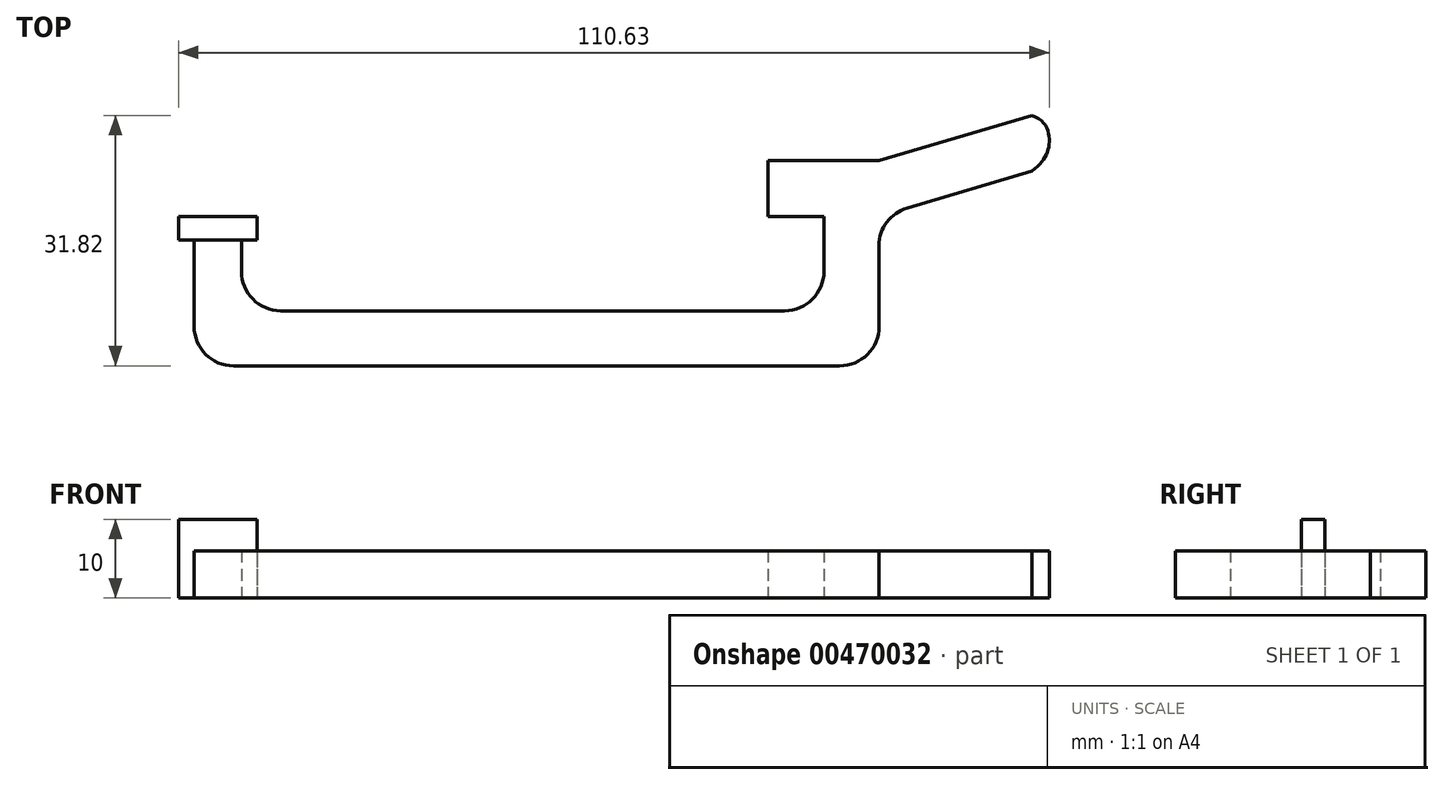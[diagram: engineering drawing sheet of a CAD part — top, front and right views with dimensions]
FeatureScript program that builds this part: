
annotation { "Feature Type Name" : "Feature", "Feature Type Description" : "" }
export const myFeature = defineFeature(function(context is Context, id is Id, definition is map)
    precondition{}
    {
        {
            var Q0;
            Q0=qCreatedBy(makeId("Top.planeOp"),FACE);
            var sketch = newSketch(context, id + "F0", { "sketchPlane" : qUnion([Q0])});
            skLineSegment(sketch, "E0.bottom", {"start": v(38.5, -3.5) * mm, "end": v(-38.5, -3.5) * mm});
            skLineSegment(sketch, "E0.top", {"start": v(38.5, 3.5) * mm, "end": v(-35.5, 3.5) * mm});
            skPoint(sketch, "E0.middle", {"position": v(0, 0) * mm});
            skLineSegment(sketch, "E1.top", {"start": v(-38.5, -3.5) * mm, "end": v(-41.5, -3.5) * mm});
            skLineSegment(sketch, "E1.right", {"start": v(-41.5, 3.5) * mm, "end": v(-41.5, -3.5) * mm});
            skLineSegment(sketch, "E2.top", {"start": v(-41.5, 12.5) * mm, "end": v(-35.5, 12.5) * mm});
            skLineSegment(sketch, "E2.left", {"start": v(-41.5, 3.5) * mm, "end": v(-41.5, 12.5) * mm});
            skLineSegment(sketch, "E2.right", {"start": v(-35.5, 3.5) * mm, "end": v(-35.5, 12.5) * mm});
            skLineSegment(sketch, "E3.bottom", {"start": v(38.5, -3.5) * mm, "end": v(45.5, -3.5) * mm});
            skLineSegment(sketch, "E3.left", {"start": v(38.5, 3.5) * mm, "end": v(38.5, 15.5) * mm});
            skLineSegment(sketch, "E3.right", {"start": v(45.5, -3.5) * mm, "end": v(45.5, 15.5) * mm});
            skLineSegment(sketch, "E4", {"start": v(38.5, 15.5) * mm, "end": v(31.4, 15.5) * mm});
            skLineSegment(sketch, "E5", {"start": v(31.4, 15.5) * mm, "end": v(31.4, 22.56) * mm});
            skLineSegment(sketch, "E6", {"start": v(31.4, 22.56) * mm, "end": v(45.5, 22.56) * mm});
            skLineSegment(sketch, "E7", {"start": v(45.5, 22.56) * mm, "end": v(64.92, 28.32) * mm});
            skLineSegment(sketch, "E8", {"start": v(45.5, 15.5) * mm, "end": v(64.92, 21.26) * mm});
            skLineSegment(sketch, "E9", {"start": v(64.92, 21.26) * mm, "end": v(64.92, 28.32) * mm});
            skPoint(sketch, "E1.bottom.start.orphan", {"position": v(-38.5, 3.5) * mm});
            skSolve(sketch);
        }
        {
            var Q0;
            Q0=makeQuery(id+"F0.imprint","IMPRINT",FACE,{"disambiguationData":[TD([[makeQuery(id+"F0.imprint","IMPRINT",EDGE,{"derivedFrom":sQuery(id+"F0.wireOp",EDGE,"E0.bottom")}),-1.0]])]});
            extrude(context, id + "F1", {"entities" : qUnion([Q0]), "depth" : 6 * mm});
        }
        {
            var Q0;
            Q0=qCreatedBy(makeId("Top.planeOp"),FACE);
            var sketch = newSketch(context, id + "F2", { "sketchPlane" : qUnion([Q0])});
            skLineSegment(sketch, "E10.0", {"start": v(-41.5, 12.5) * mm, "end": v(-35.5, 12.5) * mm});
            skLineSegment(sketch, "E11.bottom", {"start": v(-43.5, 12.5) * mm, "end": v(-33.5, 12.5) * mm});
            skLineSegment(sketch, "E11.top", {"start": v(-43.5, 15.5) * mm, "end": v(-33.5, 15.5) * mm});
            skLineSegment(sketch, "E11.left", {"start": v(-43.5, 12.5) * mm, "end": v(-43.5, 15.5) * mm});
            skLineSegment(sketch, "E11.right", {"start": v(-33.5, 12.5) * mm, "end": v(-33.5, 15.5) * mm});
            skSolve(sketch);
        }
        {
            var Q0;
            Q0=makeQuery(id+"F2.imprint","IMPRINT",FACE,{"disambiguationData":[TD([[makeQuery(id+"F2.imprint","IMPRINT",EDGE,{"derivedFrom":sQuery(id+"F2.wireOp",EDGE,"E11.top")}),-1.0]])]});
            extrude(context, id + "F3", {"entities" : qUnion([Q0]), "operationType" : NewBodyOperationType.ADD, "depth" : 10 * mm});
        }
        {
            var Q0;
            Q0=makeQuery(id+"F1.opExtrude","SWEPT_EDGE",EDGE,{"disambiguationData":[OSD([sQuery(id+"F0.wireOp",EDGE,"E2.top"),sQuery(id+"F0.wireOp",EDGE,"E2.right")])]});
            var Q1;
            Q1=makeQuery(id+"F1.opExtrude","CAP_EDGE",EDGE,{"disambiguationData":[OSD([sQuery(id+"F0.wireOp",EDGE,"E2.top")])],"isStart":false});
            var Q2;
            Q2=makeQuery(id+"F1.opExtrude","SWEPT_EDGE",EDGE,{"disambiguationData":[OSD([sQuery(id+"F0.wireOp",EDGE,"E2.top"),sQuery(id+"F0.wireOp",EDGE,"E2.left")])]});
            var Q3;
            Q3=makeQuery(id+"F1.opExtrude","SWEPT_EDGE",EDGE,{"disambiguationData":[OSD([sQuery(id+"F0.wireOp",EDGE,"E1.top"),sQuery(id+"F0.wireOp",EDGE,"E1.right")])]});
            var Q4;
            Q4=makeQuery(id+"F1.opExtrude","SWEPT_EDGE",EDGE,{"disambiguationData":[OSD([sQuery(id+"F0.wireOp",EDGE,"E3.bottom"),sQuery(id+"F0.wireOp",EDGE,"E3.right")])]});
            var Q5;
            Q5=makeQuery(id+"F1.opExtrude","SWEPT_EDGE",EDGE,{"disambiguationData":[OSD([sQuery(id+"F0.wireOp",EDGE,"E3.right"),sQuery(id+"F0.wireOp",EDGE,"E8")])]});
            fillet(context, id + "F4", {"entities" : qUnion([Q0, Q1, Q2, Q3, Q4, Q5]), "radius" : 5 * mm, "tangentPropagation" : true, "allowEdgeOverflow" : false});
        }
        {
            var Q0;
            Q0=makeQuery(id+"F1.opExtrude","SWEPT_EDGE",EDGE,{"disambiguationData":[OSD([sQuery(id+"F0.wireOp",EDGE,"E0.top"),sQuery(id+"F0.wireOp",EDGE,"E2.right")])]});
            var Q1;
            Q1=makeQuery(id+"F1.opExtrude","SWEPT_EDGE",EDGE,{"disambiguationData":[OSD([sQuery(id+"F0.wireOp",EDGE,"E0.top"),sQuery(id+"F0.wireOp",EDGE,"E3.left")])]});
            fillet(context, id + "F5", {"entities" : qUnion([Q0, Q1]), "radius" : 5 * mm, "tangentPropagation" : true, "allowEdgeOverflow" : false});
        }
        {
            var Q0;
            Q0=qCreatedBy(makeId("Top.planeOp"),FACE);
            var sketch = newSketch(context, id + "F6", { "sketchPlane" : qUnion([Q0])});
            skLineSegment(sketch, "E12.0", {"start": v(64.92, 21.26) * mm, "end": v(64.92, 28.32) * mm});
            skFitSpline(sketch, "E13", {"points": [v(64.92, 28.32) * mm, v(67.12, 24.8) * mm, v(64.92, 21.26) * mm], "startDerivative": vector(11.22, -3.8) * mm, "endDerivative": vector(-8.93, -6.75) * mm});
            skSolve(sketch);
        }
        {
            var Q0;
            Q0 = qSketchRegion(id + "F6", true);
            var Q1;
            Q1=makeQuery(id+"F1.opExtrude","CAP_FACE",FACE,{"disambiguationData":[OSD([sQuery(id+"F0.wireOp",EDGE,"E0.bottom"),sQuery(id+"F0.wireOp",EDGE,"E0.top"),sQuery(id+"F0.wireOp",EDGE,"E1.top"),sQuery(id+"F0.wireOp",EDGE,"E1.right"),sQuery(id+"F0.wireOp",EDGE,"E2.top"),sQuery(id+"F0.wireOp",EDGE,"E2.left"),sQuery(id+"F0.wireOp",EDGE,"E2.right"),sQuery(id+"F0.wireOp",EDGE,"E3.bottom"),sQuery(id+"F0.wireOp",EDGE,"E3.left"),sQuery(id+"F0.wireOp",EDGE,"E3.right"),sQuery(id+"F0.wireOp",EDGE,"E4"),sQuery(id+"F0.wireOp",EDGE,"E5"),sQuery(id+"F0.wireOp",EDGE,"E6"),sQuery(id+"F0.wireOp",EDGE,"E7"),sQuery(id+"F0.wireOp",EDGE,"E8"),sQuery(id+"F0.wireOp",EDGE,"E9")])],"isStart":false});
            extrude(context, id + "F7", {"entities" : qUnion([Q0]), "operationType" : NewBodyOperationType.ADD, "endBound" : BoundingType.UP_TO_SURFACE, "endBoundEntityFace" : qUnion([Q1]), "depth" : 25 * mm});
        }
    });
